# Revit family: ledwaterproof-batten_l12-36w-840_531000022900
name_source: partatom
category: Lighting Fixtures
units: mm (PartAtom-declared; Revit-internal decimal feet)

## family parameters
Cut with Voids When Loaded = No
Host = Face
Light Source = No
Part Type = Normal
Room Calculation Point = No
Round Connector Dimension = Use Diameter
Shared = No

## types (1)
- LEDWaterproof-Batten L12-36W-840 (1 x LED, 4000 lm, 4000)
    Apparent Load = 36 VA
    Approval mark = CE
    CIE Flux Codes = 42 71 90 91 100
    Color Rendering = 80
    Color Temperature = 4000
    Control Gear = Electronic ballast
    Default Elevation = 1800 mm
    Description = Waterproof Batten 1198mm-36W-4000lm-4000K-IP65
    Frequency = 60 Hz
    Height = 48 mm
    Lamp = 1 x LED
    Lamp Light Flux = 4000 lm
    Lamp count = 1
    Length = 1198 mm
    Luminous efficacy = 111 lm/W
    Manufacturer = OPPLE
    ModVariant = No
    Model = 531000022900
    Number of Poles = 1
    OnlyDefault = Yes
    Power Factor = 1
    Product Name = LEDWaterproof-Batten L12-36W-840
    Product group = Ceiling / wall-mounted luminaires
    ProductGroupID = 30
    Protection Class = Protection class II
    Protection Degree = IP 65
    RLX_Detail_Level = 1
    RLX_Emergency_Light_Flux = 0 lm
    RLX_Emergency_Type = 0
    RLX_Emergency_Type_DB = No
    RlxData = <blob elided: 190033 chars, md5=e6a3566b>
    Socket = socket
    Standby Power = 0 W
    System Light Flux = 4000 lm
    System Power = 36 W
    Type Comments = Product without accessories
    Type Image = web_wp_bat_e.jpg
    URL = http://relux.com
    VarID = ---
    Voltage = 230 V
    Voltage Range = 220-240 V
    Weight = 0.00 kg
    Width = 48 mm

## geometry (parser evidence)
native form markers: Blend x4, Sweep x14
no freeform markers — native parametric forms only
